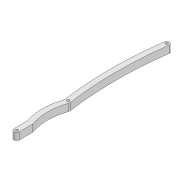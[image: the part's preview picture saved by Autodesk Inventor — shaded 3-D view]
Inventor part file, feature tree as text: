
AUTODESK INVENTOR PART (.ipt)
format: ipt  version: 2022 (Build 260153000, 153)  size: 119,296 bytes
history: native  units: mm
features: extrude x1, fillet x1, sketch x1
ambient origin geometry x8: Origin, YZ Plane, XZ Plane, XY Plane, X Axis, Y Axis, Z Axis, Center Point
bodies: Solid1 (feature_tree)
feature tree (3):
  extrude  "Extrusion1"  Depth=6.0mm
  fillet  "Fillet1"  Radius=3.0mm
  sketch  "Sketch1"  dims[d0=167.039mm d1=6.0mm d2=3.0mm d3=3.0mm d4=8.0mm d5=0.0mm d10=3.0mm d11=57.227mm d12=400.0mm d13=400.0mm d16=15.0mm d17=55.0mm d18=50.0mm d19=50.0mm d20=10.0mm]
